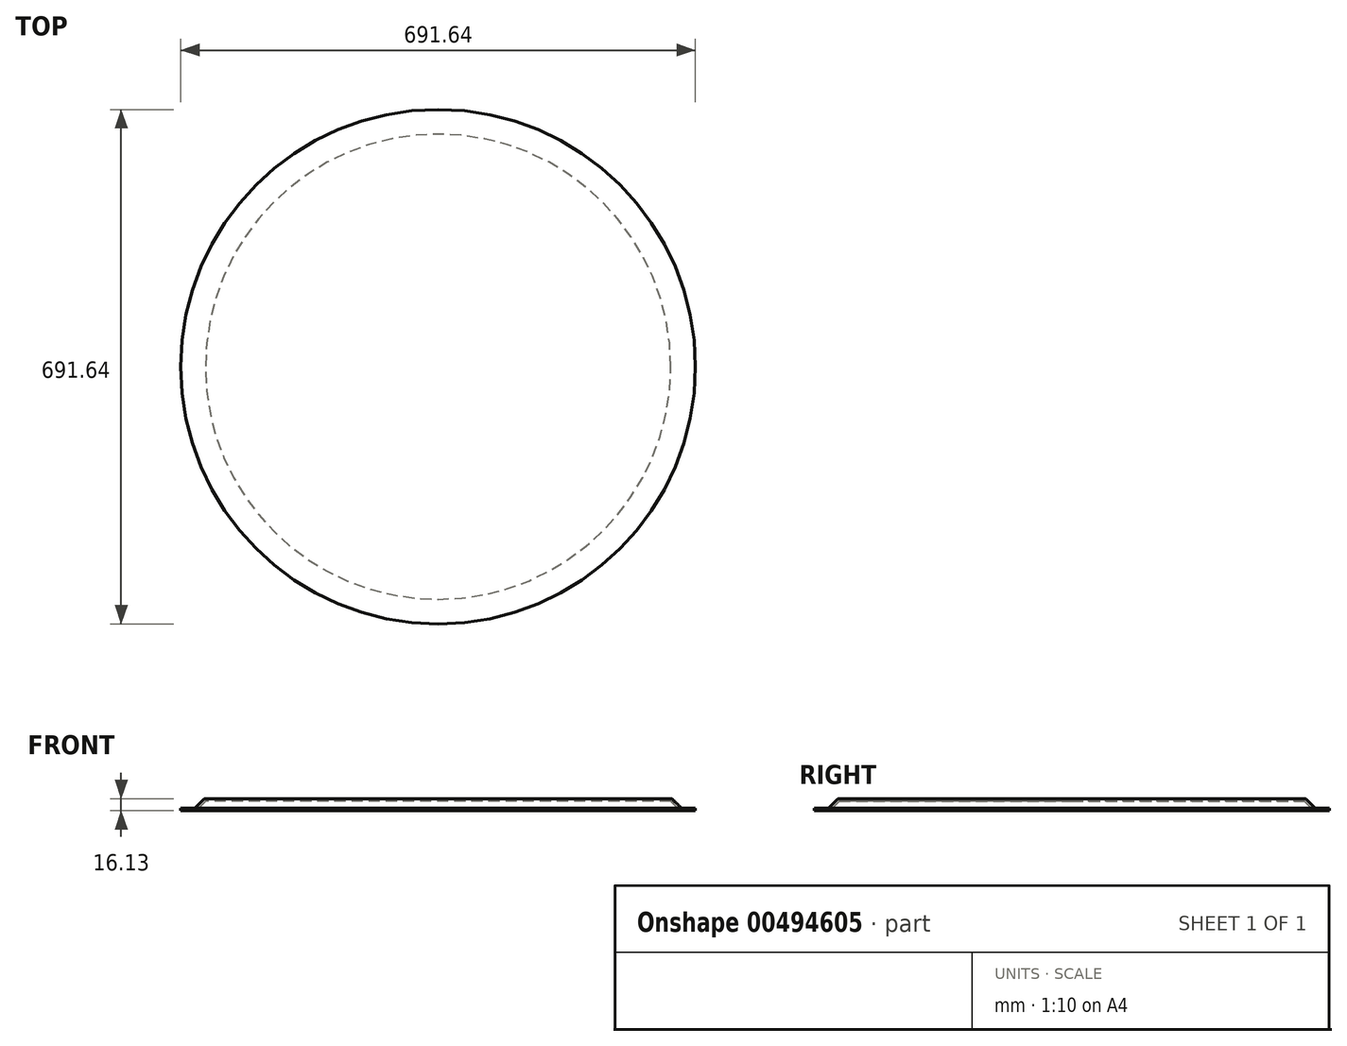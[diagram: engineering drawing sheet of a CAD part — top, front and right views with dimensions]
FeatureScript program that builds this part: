
annotation { "Feature Type Name" : "Feature", "Feature Type Description" : "" }
export const myFeature = defineFeature(function(context is Context, id is Id, definition is map)
    precondition{}
    {
        {
            var Q0;
            Q0=qCreatedBy(makeId("Front.planeOp"),FACE);
            var sketch = newSketch(context, id + "F0", { "sketchPlane" : qUnion([Q0])});
            skLineSegment(sketch, "E0", {"start": v(0, 0) * mm, "end": v(-312.76, 0) * mm});
            skLineSegment(sketch, "E1", {"start": v(-315, -0.93) * mm, "end": v(-325.84, -11.77) * mm});
            skLineSegment(sketch, "E2", {"start": v(-328.09, -12.7) * mm, "end": v(-345.82, -12.7) * mm});
            skPoint(sketch, "E3.visualSharp", {"position": v(-314.07, 0) * mm});
            skArc(sketch, "E3.filletArc", {"start": v(-312.76, 0) * mm, "mid": v(-313.97, -0.24) * mm, "end": v(-315, -0.93) * mm});
            skPoint(sketch, "E4.visualSharp", {"position": v(-326.77, -12.7) * mm});
            skArc(sketch, "E4.filletArc", {"start": v(-328.09, -12.7) * mm, "mid": v(-326.87, -12.46) * mm, "end": v(-325.84, -11.77) * mm});
            skLineSegment(sketch, "E5.0", {"start": v(-328.09, -16.13) * mm, "end": v(-345.82, -16.13) * mm});
            skArc(sketch, "E5.1", {"start": v(-328.09, -16.13) * mm, "mid": v(-325.56, -15.63) * mm, "end": v(-323.42, -14.2) * mm});
            skLineSegment(sketch, "E5.2", {"start": v(-312.65, -3.43) * mm, "end": v(-323.42, -14.2) * mm});
            skLineSegment(sketch, "E5.3", {"start": v(0, -3.43) * mm, "end": v(-312.65, -3.43) * mm});
            skLineSegment(sketch, "E6", {"start": v(-345.82, -12.7) * mm, "end": v(-345.82, -16.13) * mm});
            skLineSegment(sketch, "E7", {"start": v(0, 0) * mm, "end": v(0, -3.43) * mm});
            skSolve(sketch);
        }
        {
            var Q0;
            Q0 = qSketchRegion(id + "F0", true);
            var Q1;
            Q1=sQuery(id+"F0.wireOp",EDGE,"E7");
            revolve(context, id + "F1", {"entities" : qUnion([Q0]), "axis" : qUnion([Q1]), "revolveType" : RevolveType.FULL});
        }
    });
